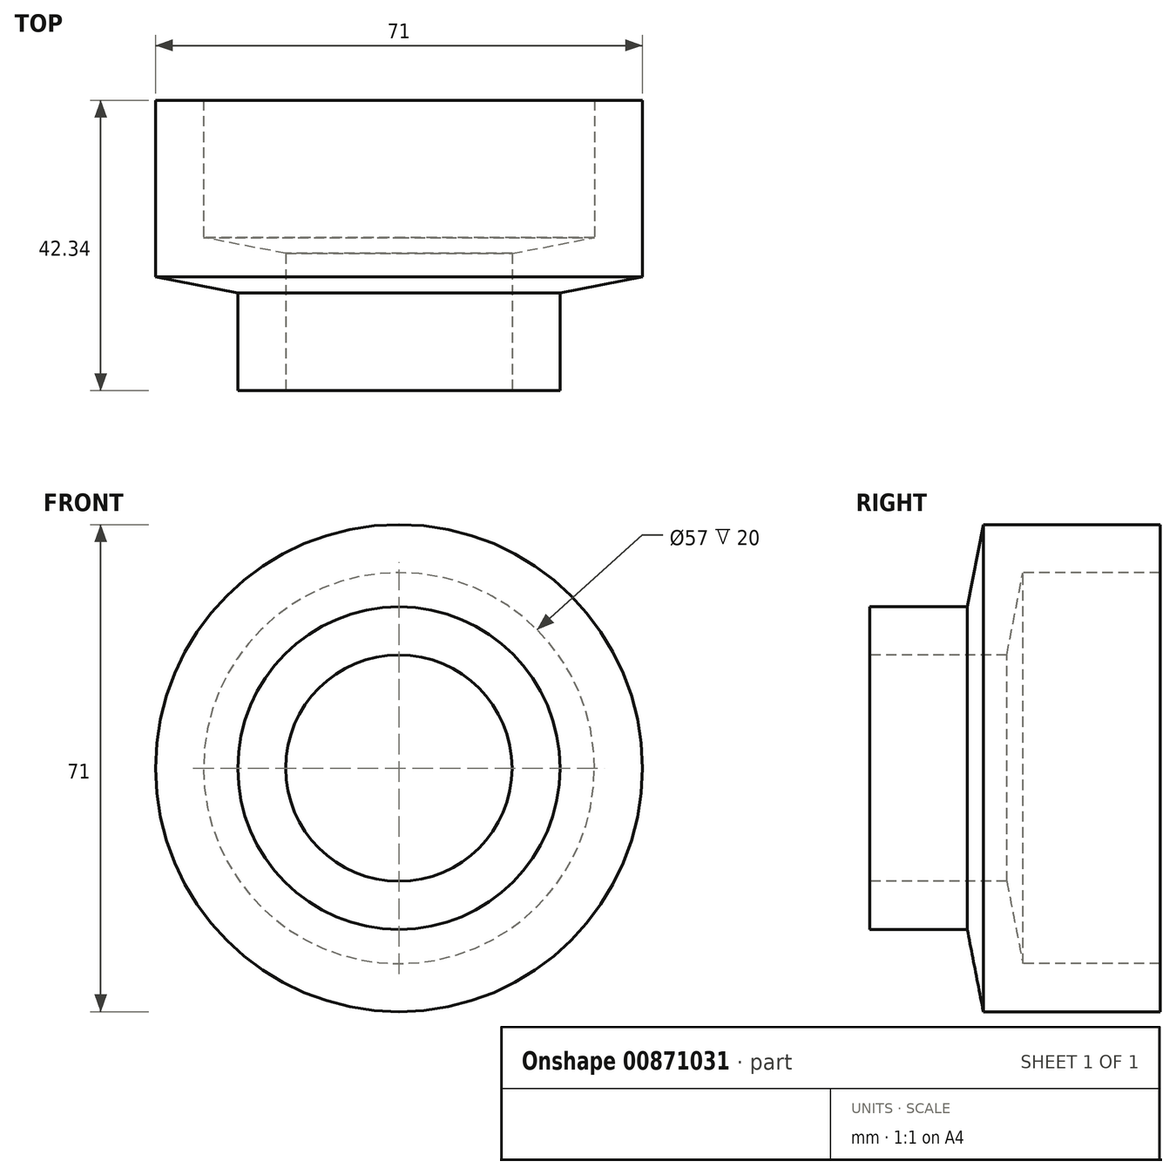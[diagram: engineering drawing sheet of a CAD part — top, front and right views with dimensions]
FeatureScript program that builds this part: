
annotation { "Feature Type Name" : "Feature", "Feature Type Description" : "" }
export const myFeature = defineFeature(function(context is Context, id is Id, definition is map)
    precondition{}
    {
        {
            var Q0;
            Q0=qCreatedBy(makeId("Top.planeOp"),FACE);
            var sketch = newSketch(context, id + "F0", { "sketchPlane" : qUnion([Q0])});
            skLineSegment(sketch, "E0", {"start": v(0, 0) * mm, "end": v(0, 73.33) * mm, "construction": true});
            skLineSegment(sketch, "E1", {"start": v(28.5, 60.36) * mm, "end": v(28.5, 40.36) * mm});
            skLineSegment(sketch, "E2", {"start": v(16.5, 38.02) * mm, "end": v(16.5, 18.02) * mm});
            skLineSegment(sketch, "E3", {"start": v(16.5, 38.02) * mm, "end": v(28.5, 40.36) * mm});
            skLineSegment(sketch, "E4.0", {"start": v(23.5, 32.25) * mm, "end": v(23.5, 18.02) * mm});
            skLineSegment(sketch, "E4.1", {"start": v(23.5, 32.25) * mm, "end": v(35.5, 34.59) * mm});
            skLineSegment(sketch, "E4.2", {"start": v(35.5, 60.36) * mm, "end": v(35.5, 34.59) * mm});
            skLineSegment(sketch, "E5", {"start": v(16.5, 18.02) * mm, "end": v(23.5, 18.02) * mm});
            skLineSegment(sketch, "E6", {"start": v(28.5, 60.36) * mm, "end": v(35.5, 60.36) * mm});
            skSolve(sketch);
        }
        {
            var Q0;
            Q0=makeQuery(id+"F0.imprint","IMPRINT",FACE,{"disambiguationData":[TD([[makeQuery(id+"F0.imprint","IMPRINT",EDGE,{"derivedFrom":sQuery(id+"F0.wireOp",EDGE,"E1")}),1.0]])]});
            var Q1;
            Q1=sQuery(id+"F0.wireOp",EDGE,"E0");
            revolve(context, id + "F1", {"surfaceOperationType" : NewSurfaceOperationType.NEW, "entities" : qUnion([Q0]), "axis" : qUnion([Q1]), "revolveType" : RevolveType.FULL});
        }
    });
